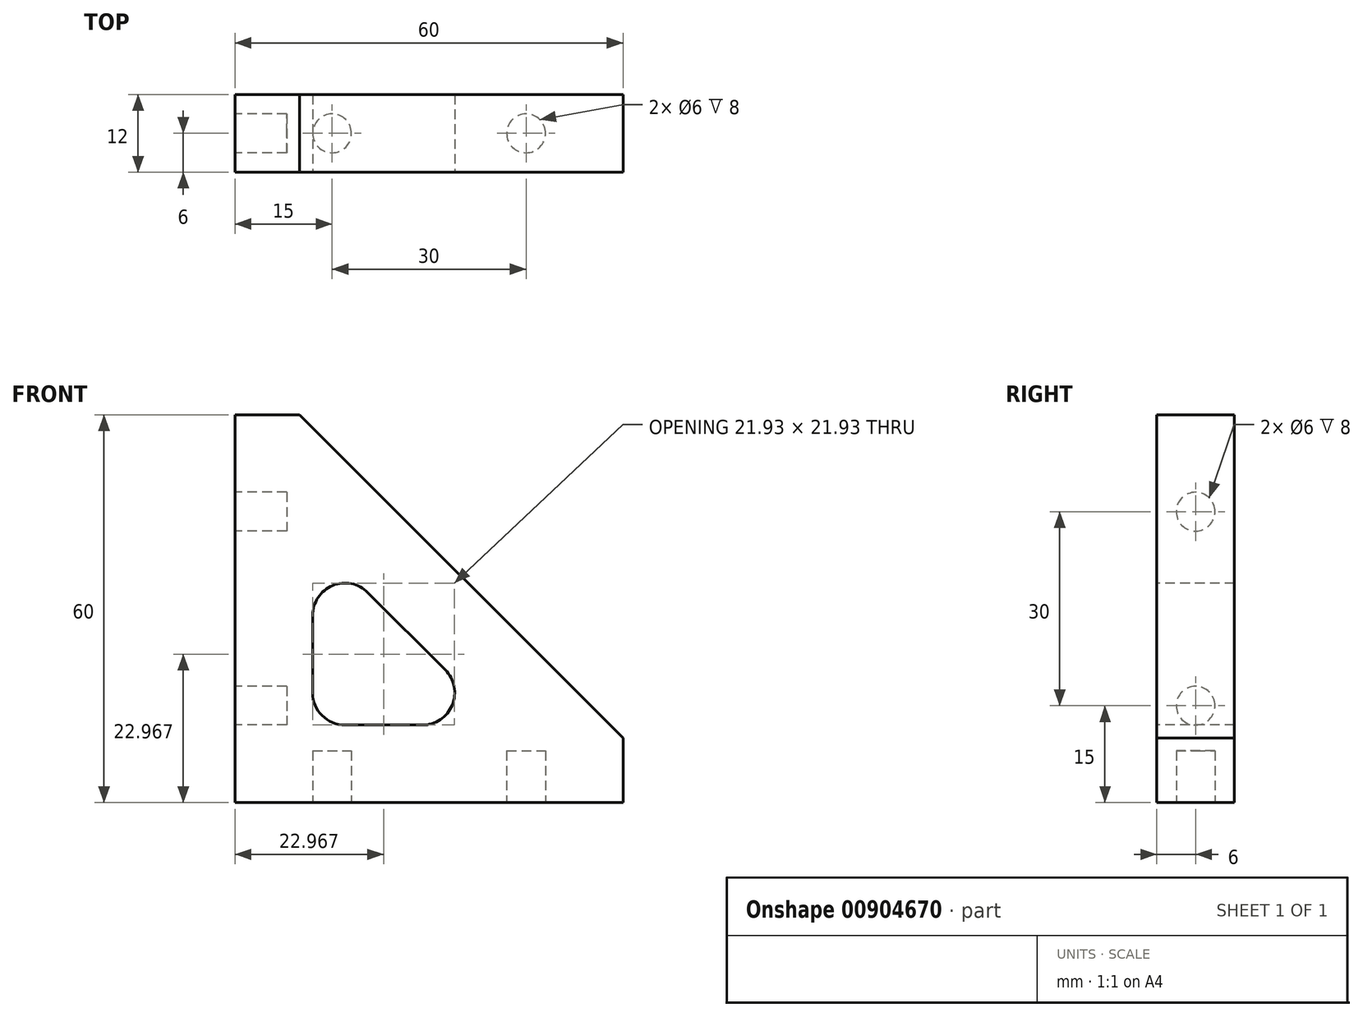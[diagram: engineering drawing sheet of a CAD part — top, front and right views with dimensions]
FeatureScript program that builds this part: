
annotation { "Feature Type Name" : "Feature", "Feature Type Description" : "" }
export const myFeature = defineFeature(function(context is Context, id is Id, definition is map)
    precondition{}
    {
        {
            var Q0;
            Q0=qCreatedBy(makeId("Front.planeOp"),FACE);
            var sketch = newSketch(context, id + "F0", { "sketchPlane" : qUnion([Q0])});
            skLineSegment(sketch, "E0.bottom", {"start": v(0, 0) * mm, "end": v(60, 0) * mm});
            skLineSegment(sketch, "E0.top", {"start": v(0, 60) * mm, "end": v(60, 60) * mm});
            skLineSegment(sketch, "E0.left", {"start": v(0, 0) * mm, "end": v(0, 60) * mm});
            skLineSegment(sketch, "E0.right", {"start": v(60, 0) * mm, "end": v(60, 60) * mm});
            skSolve(sketch);
        }
        {
            var Q0;
            Q0=makeQuery(id+"F0.imprint","IMPRINT",FACE,{"disambiguationData":[TD([[makeQuery(id+"F0.imprint","IMPRINT",EDGE,{"derivedFrom":sQuery(id+"F0.wireOp",EDGE,"E0.bottom")}),1.0]])]});
            extrude(context, id + "F1", {"entities" : qUnion([Q0]), "depth" : 12 * mm, "offsetDistance" : 25 * mm});
        }
        {
            var Q0;
            Q0=makeQuery(id+"F1.opExtrude","CAP_FACE",FACE,{"disambiguationData":[OSD([sQuery(id+"F0.wireOp",EDGE,"E0.bottom"),sQuery(id+"F0.wireOp",EDGE,"E0.top"),sQuery(id+"F0.wireOp",EDGE,"E0.left"),sQuery(id+"F0.wireOp",EDGE,"E0.right")])],"isStart":false});
            var sketch = newSketch(context, id + "F2", { "sketchPlane" : qUnion([Q0])});
            skLineSegment(sketch, "E1", {"start": v(60, 60) * mm, "end": v(10, 60) * mm});
            skLineSegment(sketch, "E2", {"start": v(10, 60) * mm, "end": v(60, 10) * mm});
            skLineSegment(sketch, "E3", {"start": v(60, 10) * mm, "end": v(60, 60) * mm});
            skSolve(sketch);
        }
        {
            var Q0;
            Q0=makeQuery(id+"F2.imprint","IMPRINT",FACE,{"disambiguationData":[TD([[makeQuery(id+"F2.imprint","IMPRINT",EDGE,{"derivedFrom":sQuery(id+"F2.wireOp",EDGE,"E1")}),-1.0]])]});
            extrude(context, id + "F3", {"entities" : qUnion([Q0]), "operationType" : NewBodyOperationType.REMOVE, "endBound" : BoundingType.THROUGH_ALL, "oppositeDirection" : true, "depth" : 25 * mm, "offsetDistance" : 25 * mm});
        }
        {
            var Q0;
            Q0=makeQuery(id+"F1.opExtrude","CAP_FACE",FACE,{"disambiguationData":[OSD([sQuery(id+"F0.wireOp",EDGE,"E0.bottom"),sQuery(id+"F0.wireOp",EDGE,"E0.top"),sQuery(id+"F0.wireOp",EDGE,"E0.left"),sQuery(id+"F0.wireOp",EDGE,"E0.right")])],"isStart":false});
            var sketch = newSketch(context, id + "F4", { "sketchPlane" : qUnion([Q0])});
            skLineSegment(sketch, "E4.0", {"start": v(20.54, 32.5) * mm, "end": v(32.5, 20.54) * mm});
            skLineSegment(sketch, "E5.0", {"start": v(12, 17) * mm, "end": v(12, 28.96) * mm});
            skLineSegment(sketch, "E6.0", {"start": v(17, 12) * mm, "end": v(28.96, 12) * mm});
            skArc(sketch, "E7.filletArc", {"start": v(20.54, 32.5) * mm, "mid": v(15.09, 33.58) * mm, "end": v(12, 28.96) * mm});
            skArc(sketch, "E8.filletArc", {"start": v(12, 17) * mm, "mid": v(13.46, 13.46) * mm, "end": v(17, 12) * mm});
            skArc(sketch, "E9.filletArc", {"start": v(28.96, 12) * mm, "mid": v(33.58, 15.09) * mm, "end": v(32.5, 20.54) * mm});
            skSolve(sketch);
        }
        {
            var Q0;
            Q0=makeQuery(id+"F4.imprint","IMPRINT",FACE,{"disambiguationData":[TD([[makeQuery(id+"F4.imprint","IMPRINT",EDGE,{"derivedFrom":sQuery(id+"F4.wireOp",EDGE,"E4.0")}),-1.0]])]});
            extrude(context, id + "F5", {"entities" : qUnion([Q0]), "operationType" : NewBodyOperationType.REMOVE, "endBound" : BoundingType.THROUGH_ALL, "oppositeDirection" : true, "depth" : 25 * mm, "offsetDistance" : 25 * mm});
        }
        {
            var Q0;
            Q0=makeQuery(id+"F1.opExtrude","SWEPT_FACE",FACE,{"disambiguationData":[OSD([sQuery(id+"F0.wireOp",EDGE,"E0.left")])]});
            var sketch = newSketch(context, id + "F6", { "sketchPlane" : qUnion([Q0])});
            skLineSegment(sketch, "E10.0", {"start": v(6, 0) * mm, "end": v(6, 60) * mm, "construction": true});
            skLineSegment(sketch, "E11.0", {"start": v(12, 15) * mm, "end": v(0, 15) * mm, "construction": true});
            skLineSegment(sketch, "E12.0", {"start": v(12, 45) * mm, "end": v(0, 45) * mm, "construction": true});
            skCircle(sketch, "E13", {"center": v(6, 45) * mm, "radius": 3 * mm});
            skCircle(sketch, "E14", {"center": v(6, 15) * mm, "radius": 3 * mm});
            skSolve(sketch);
        }
        {
            var Q0;
            Q0=makeQuery(id+"F6.imprint","IMPRINT",FACE,{"disambiguationData":[TD([[makeQuery(id+"F6.imprint","IMPRINT",EDGE,{"derivedFrom":sQuery(id+"F6.wireOp",EDGE,"E13")}),1.0]])]});
            var Q1;
            Q1=makeQuery(id+"F6.imprint","IMPRINT",FACE,{"disambiguationData":[TD([[makeQuery(id+"F6.imprint","IMPRINT",EDGE,{"derivedFrom":sQuery(id+"F6.wireOp",EDGE,"E14")}),1.0]])]});
            extrude(context, id + "F7", {"entities" : qUnion([Q0, Q1]), "operationType" : NewBodyOperationType.REMOVE, "oppositeDirection" : true, "depth" : 8 * mm, "offsetDistance" : 25 * mm});
        }
        {
            var Q0;
            Q0=makeQuery(id+"F1.opExtrude","SWEPT_FACE",FACE,{"disambiguationData":[OSD([sQuery(id+"F0.wireOp",EDGE,"E0.bottom")])]});
            var sketch = newSketch(context, id + "F8", { "sketchPlane" : qUnion([Q0])});
            skLineSegment(sketch, "E15.0", {"start": v(0, 6) * mm, "end": v(60, 6) * mm, "construction": true});
            skLineSegment(sketch, "E16.0", {"start": v(15, 12) * mm, "end": v(15, 0) * mm, "construction": true});
            skLineSegment(sketch, "E17.0", {"start": v(45, 12) * mm, "end": v(45, 0) * mm, "construction": true});
            skCircle(sketch, "E18", {"center": v(15, 6) * mm, "radius": 3 * mm});
            skCircle(sketch, "E19", {"center": v(45, 6) * mm, "radius": 3 * mm});
            skSolve(sketch);
        }
        {
            var Q0;
            Q0=makeQuery(id+"F8.imprint","IMPRINT",FACE,{"disambiguationData":[TD([[makeQuery(id+"F8.imprint","IMPRINT",EDGE,{"derivedFrom":sQuery(id+"F8.wireOp",EDGE,"E18")}),1.0]])]});
            var Q1;
            Q1=makeQuery(id+"F8.imprint","IMPRINT",FACE,{"disambiguationData":[TD([[makeQuery(id+"F8.imprint","IMPRINT",EDGE,{"derivedFrom":sQuery(id+"F8.wireOp",EDGE,"E19")}),1.0]])]});
            extrude(context, id + "F9", {"entities" : qUnion([Q0, Q1]), "operationType" : NewBodyOperationType.REMOVE, "oppositeDirection" : true, "depth" : 8 * mm, "offsetDistance" : 25 * mm});
        }
    });
